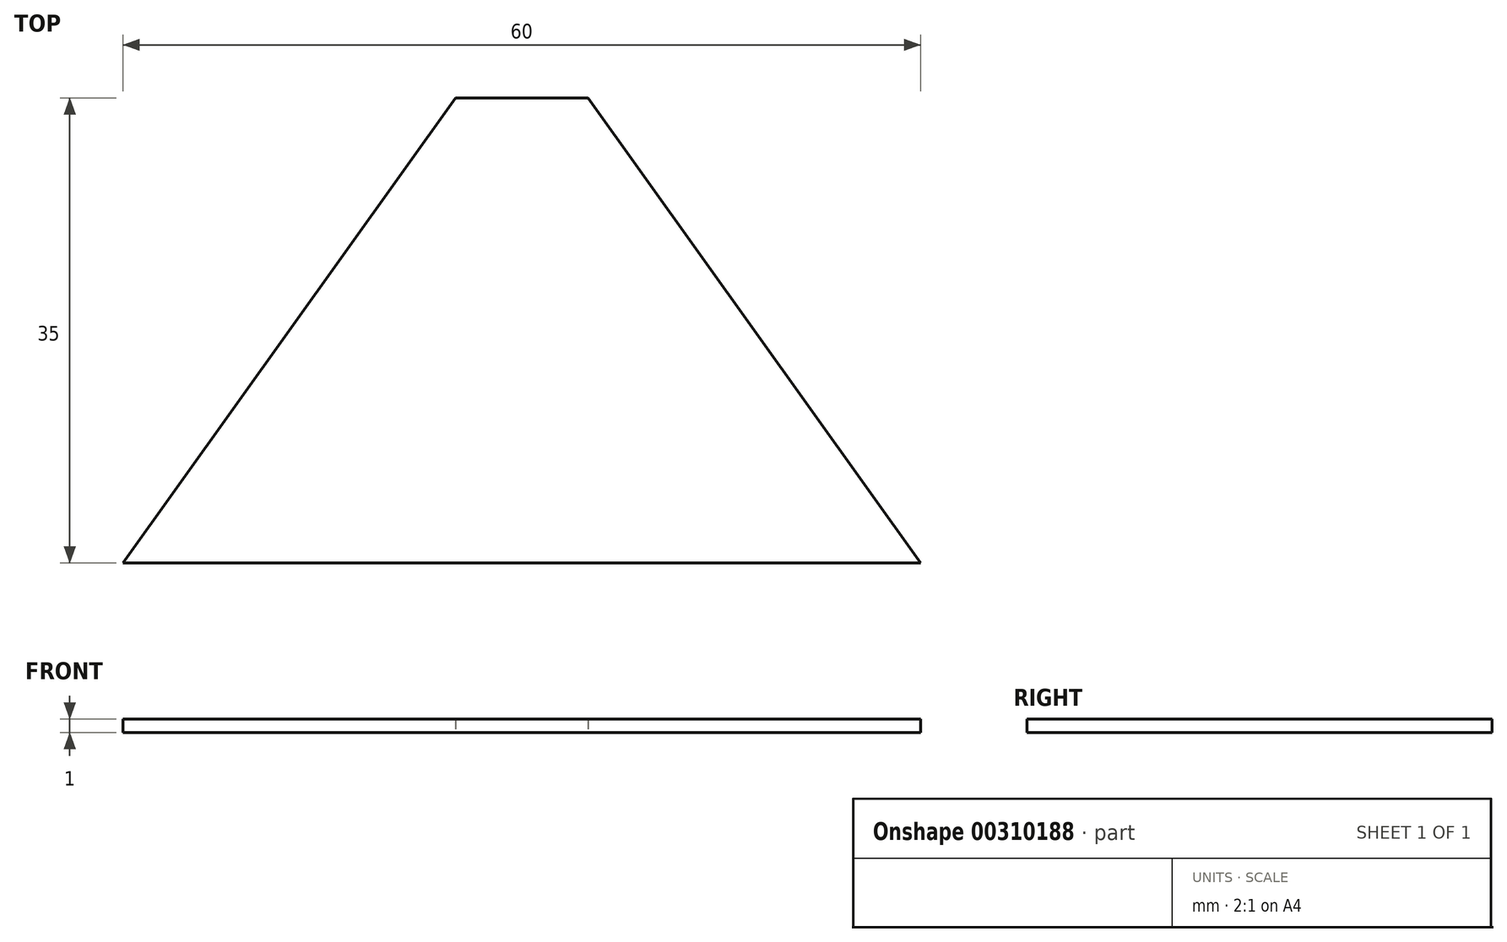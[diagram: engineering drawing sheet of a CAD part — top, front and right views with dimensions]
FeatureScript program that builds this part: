
annotation { "Feature Type Name" : "Feature", "Feature Type Description" : "" }
export const myFeature = defineFeature(function(context is Context, id is Id, definition is map)
    precondition{}
    {
        {
            var Q0;
            Q0=qCreatedBy(makeId("Top.planeOp"),FACE);
            var sketch = newSketch(context, id + "F0", { "sketchPlane" : qUnion([Q0])});
            skLineSegment(sketch, "E0", {"start": v(0, 0) * mm, "end": v(0, 35) * mm, "construction": true});
            skLineSegment(sketch, "E1", {"start": v(0, 35) * mm, "end": v(-5, 35) * mm});
            skLineSegment(sketch, "E2", {"start": v(-5, 35) * mm, "end": v(-30, 0) * mm});
            skLineSegment(sketch, "E3", {"start": v(-30, 0) * mm, "end": v(0, 0) * mm});
            skLineSegment(sketch, "E4.MirrorCS", {"start": v(0, 35) * mm, "end": v(5, 35) * mm});
            skLineSegment(sketch, "E5.MirrorCS", {"start": v(30, 0) * mm, "end": v(0, 0) * mm});
            skLineSegment(sketch, "E6.MirrorCS", {"start": v(5, 35) * mm, "end": v(30, 0) * mm});
            skSolve(sketch);
        }
        {
            var Q0;
            Q0 = qSketchRegion(id + "F0", true);
            extrude(context, id + "F1", {"entities" : qUnion([Q0]), "depth" : 1 * mm});
        }
    });
